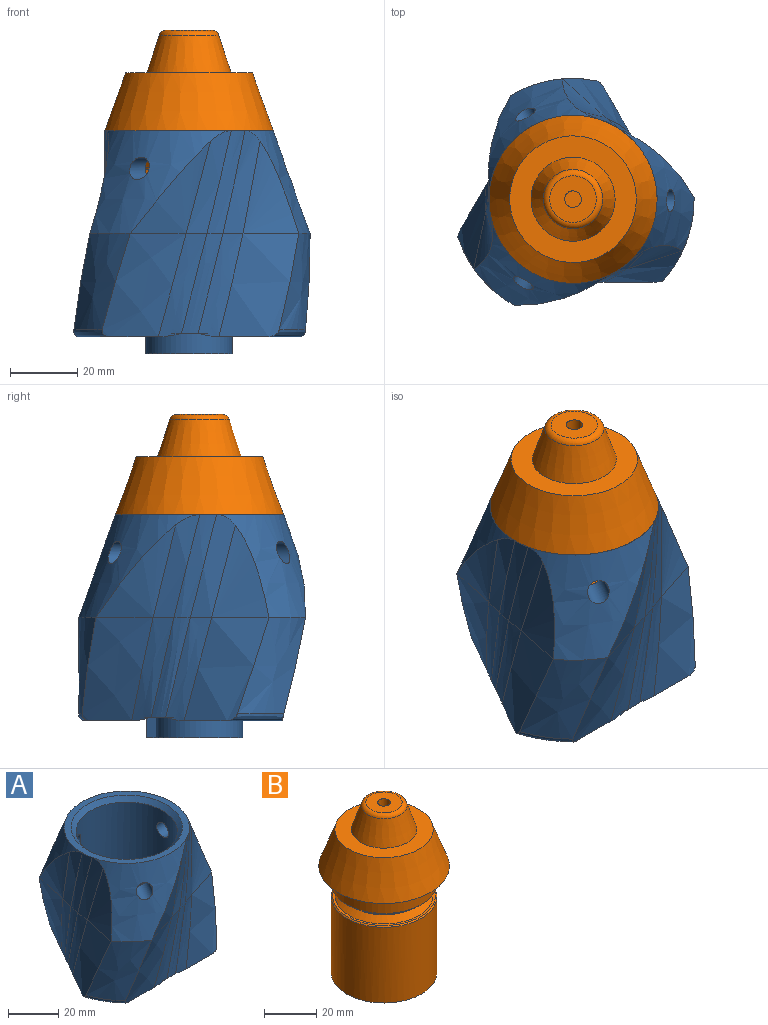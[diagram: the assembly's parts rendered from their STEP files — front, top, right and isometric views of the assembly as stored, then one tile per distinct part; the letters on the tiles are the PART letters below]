
ASSEMBLY  parts=2 mates=1
PART A: 59 faces, bbox 76.5x72.6x102.4 mm
  f0: cylinder r=20.2mm len=48mm, axis (0,0,1), area 5988.6mm2, adj f51,f54,f55,f56,f57
  f1: cone r=5.67mm half-angle=19.8deg, axis (0,0,-1), area 869.8mm2, adj f14,f32,f33,f34,f35,f47,f56
  f2: cone r=5.67mm half-angle=19.8deg, axis (0,0,-1), area 869.8mm2, adj f17,f37,f38,f39,f40,f47,f55
  f3: cone r=5.67mm half-angle=19.8deg, axis (0,0,-1), area 874.8mm2, adj f11,f27,f28,f29,f30,f47,f54
  f4: plane 50.05x50mm, normal (0,0,-1), area 1420.5mm2, adj f7,f8,f19,f44,f45,f46,f48,f49
  f5: plane 33.99x14.32mm, normal (0,0,-1), area 213.8mm2, adj f16,f18,f20,f21,f41,f46
  f6: plane 29.44x24.55mm, normal (0,0,-1), area 213.8mm2, adj f10,f12,f24,f25,f43,f45
  f7: bspline ~43.86x19.6mm, area 148.3mm2, adj f4,f23,f24,f31
  f8: bspline ~43.86x14.74mm, area 148.3mm2, adj f4,f21,f22,f36
  f9: plane 29.44x24.5mm, normal (0,0,-1), area 213.8mm2, adj f13,f15,f22,f23,f42,f44
  f10: bspline ~43.86x32.62mm, area 541.6mm2, adj f6,f11,f25,f28,f43
  f11: bspline ~43.86x23.02mm, area 468.9mm2, adj f3,f10,f12,f43
  f12: bspline ~43.86x32.74mm, area 538.4mm2, adj f6,f11,f24,f29,f43
  f13: bspline ~43.86x29.67mm, area 541.6mm2, adj f9,f14,f23,f33,f42
  f14: bspline ~43.86x30.01mm, area 468.9mm2, adj f1,f13,f15,f42
  f15: bspline ~43.86x28.16mm, area 538.4mm2, adj f9,f14,f22,f34,f42
  f16: bspline ~30.7x19.96mm, area 541.6mm2, adj f5,f17,f21,f38,f41
  f17: bspline ~43.86x30.62mm, area 468.9mm2, adj f2,f16,f18,f41
  f18: bspline ~43.86x28.55mm, area 538.4mm2, adj f5,f17,f20,f39,f41
  f19: bspline ~43.86x19.21mm, area 148.3mm2, adj f4,f20,f25,f26
  f20: bspline ~42.73x13.58mm, area 194.6mm2, adj f5,f18,f19,f40,f46
  f21: bspline ~40.16x11mm, area 194.3mm2, adj f5,f8,f16,f37,f46
  f22: bspline ~42.73x13.22mm, area 194.6mm2, adj f8,f9,f15,f35,f44
  f23: bspline ~40.16x13.92mm, area 194.3mm2, adj f7,f9,f13,f32,f44
  f24: bspline ~42.73x15.47mm, area 194.6mm2, adj f6,f7,f12,f30,f45
  f25: bspline ~40.16x14.39mm, area 194.3mm2, adj f6,f10,f19,f27,f45
  f26: bspline ~43.86x15.95mm, area 153.2mm2, adj f19,f27,f40,f47
  f27: bspline ~66.67x22.13mm, area 189.1mm2, adj f3,f25,f26,f28,f47
  f28: bspline ~27.47x24.44mm, area 242.5mm2, adj f3,f10,f27
  f29: bspline ~43.86x28mm, area 242.6mm2, adj f3,f12,f30
  f30: bspline ~30.56x13.43mm, area 189.2mm2, adj f3,f24,f29,f31,f47
  f31: bspline ~43.86x13.69mm, area 153.1mm2, adj f7,f30,f32,f47
  f32: bspline ~30.56x11.53mm, area 189.1mm2, adj f1,f23,f31,f33,f47
  f33: bspline ~27.47x19.53mm, area 242.5mm2, adj f1,f13,f32
  f34: bspline ~43.86x20.58mm, area 242.6mm2, adj f1,f15,f35
  f35: bspline ~30.56x10.61mm, area 189.2mm2, adj f1,f22,f34,f36,f47
  f36: bspline ~30.56x10.64mm, area 153.2mm2, adj f8,f35,f37,f47
  f37: bspline ~66.67x22.54mm, area 189.1mm2, adj f2,f21,f36,f38,f47
  f38: bspline ~27.47x22.79mm, area 242.5mm2, adj f2,f16,f37
  f39: bspline ~43.86x28.04mm, area 242.6mm2, adj f2,f18,f40
  f40: bspline ~66.67x23.05mm, area 189.2mm2, adj f2,f20,f26,f39,f47
  f41: bspline ~31.33x5.49mm, area 56.1mm2, adj f5,f16,f17,f18
  f42: bspline ~28.87x15.09mm, area 56.1mm2, adj f9,f13,f14,f15
  f43: bspline ~28.74x15.4mm, area 56.1mm2, adj f6,f10,f11,f12
  f44: torus R=26mm, axis (0,0,1), area 66.1mm2, adj f4,f9,f22,f23
  f45: torus R=26mm, axis (0,0,1), area 66.1mm2, adj f4,f6,f24,f25
  f46: torus R=26mm, axis (0,0,1), area 66.1mm2, adj f4,f5,f20,f21
  f47: plane 50.01x50.01mm, normal (0,0,1), area 415.3mm2, adj f1,f2,f3,f26,f27,f30,f31,f32
  f48: plane 6x2.86mm, normal (0.95,-0.3,0), area 18mm2, adj f4,f49,f53,f58
  f49: plane 7.44x6mm, normal (0.3,0.95,0), area 46.8mm2, adj f4,f48,f50,f58
  f50: plane 6x2.86mm, normal (-0.95,0.3,0), area 18mm2, adj f4,f49,f53,f58
  f51: plane 40.4x40.4mm, normal (0,0,1), area 961.4mm2, adj f0,f52
  f52: cylinder r=10.1mm len=20.2mm, axis (0,0,-1), area 1031.9mm2, adj f51,f58
  f53: cylinder r=12.9mm len=25.8mm, axis (0,0,-1), area 438.8mm2, adj f4,f48,f50,f58
  f54: cylinder r=3.32mm len=12.22mm, axis (0.51,0.86,0), area 200.6mm2, adj f0,f3
  f55: cylinder r=3.32mm len=11.12mm, axis (0.49,-0.87,0), area 187.6mm2, adj f0,f2
  f56: cylinder r=3.32mm len=9.62mm, axis (-1,0.01,0), area 196.3mm2, adj f0,f1
  f57: cone r=20.2mm half-angle=45deg, axis (0,0,1), area 376.8mm2, adj f0,f47
  f58: plane 28.66x25.8mm, normal (0,0,-1), area 222.6mm2, adj f48,f49,f50,f52,f53
PART B: 26 faces, bbox 50x50x79.8 mm
  f0: cylinder r=20.2mm len=40.4mm, axis (0,0,1), area 763.1mm2, adj f21,f22
  f1: plane 50x50mm, normal (0,0,-1), area 415.2mm2, adj f2,f22
  f2: cone r=25mm half-angle=19.8deg, axis (0,0,-1), area 2511.7mm2, adj f1,f3
  f3: plane 37.64x37.64mm, normal (0,0,1), area 621.9mm2, adj f2,f4
  f4: cone r=12.5mm half-angle=18.1deg, axis (0,0,-1), area 791.1mm2, adj f3,f23
  f5: plane 13.85x13.85mm, normal (0,0,1), area 131.7mm2, adj f6,f23
  f6: cylinder r=2.46mm len=20mm, axis (0,0,1), area 309.1mm2, adj f5,f7
  f7: plane 4.92x4.92mm, normal (0,0,1), area 19mm2, adj f6
  f8: plane 39.4x39.4mm, normal (0,0,-1), area 120.6mm2, adj f21,f25
  f9: cylinder r=16.2mm len=32.4mm, axis (0,0,-1), area 50.9mm2, adj f24,f25
  f10: plane 39.4x39.4mm, normal (0,0,1), area 120.6mm2, adj f20,f24
  f11: plane 34.87x30.2mm, normal (0,0,-1), area 789.8mm2, adj f12,f13,f14,f15,f16,f17
  f12: plane 30x15.1mm, normal (0.87,0.5,0), area 523.1mm2, adj f11,f13,f17,f18
  f13: plane 30x15.1mm, normal (0.87,-0.5,0), area 523.1mm2, adj f11,f12,f14,f18
  f14: plane 30x17.44mm, normal (0,-1,0), area 523.1mm2, adj f11,f13,f15,f18
  f15: plane 30x15.1mm, normal (-0.87,-0.5,0), area 523.1mm2, adj f11,f14,f16,f18
  f16: plane 30x15.1mm, normal (-0.87,0.5,0), area 523.1mm2, adj f11,f15,f17,f18
  f17: plane 30x17.44mm, normal (0,1,0), area 523.1mm2, adj f11,f12,f16,f18
  f18: plane 40.4x40.4mm, normal (0,0,-1), area 492mm2, adj f12,f13,f14,f15,f16,f17,f19
  f19: cylinder r=20.2mm len=40.4mm, axis (0,0,1), area 4504.1mm2, adj f18,f20
  f20: cone r=20.2mm half-angle=45deg, axis (0,0,-1), area 88.6mm2, adj f10,f19
  f21: cone r=19.7mm half-angle=45deg, axis (0,0,1), area 88.6mm2, adj f0,f8
  f22: cone r=22.2mm half-angle=45deg, axis (0,0,1), area 376.8mm2, adj f0,f1
  f23: torus R=6.93mm, axis (0,0,-1), area 126.5mm2, adj f4,f5
  f24: cone r=18.7mm half-angle=45deg, axis (0,0,-1), area 387.6mm2, adj f9,f10
  f25: cone r=16.2mm half-angle=45deg, axis (0,0,1), area 387.6mm2, adj f8,f9
PLACE A at identity fixed
PLACE B t=(0,0,61.26)mm
MATE slider B.f0 <-> A.f0  axis (0,0,-1) through (0,0,11.26)mm
